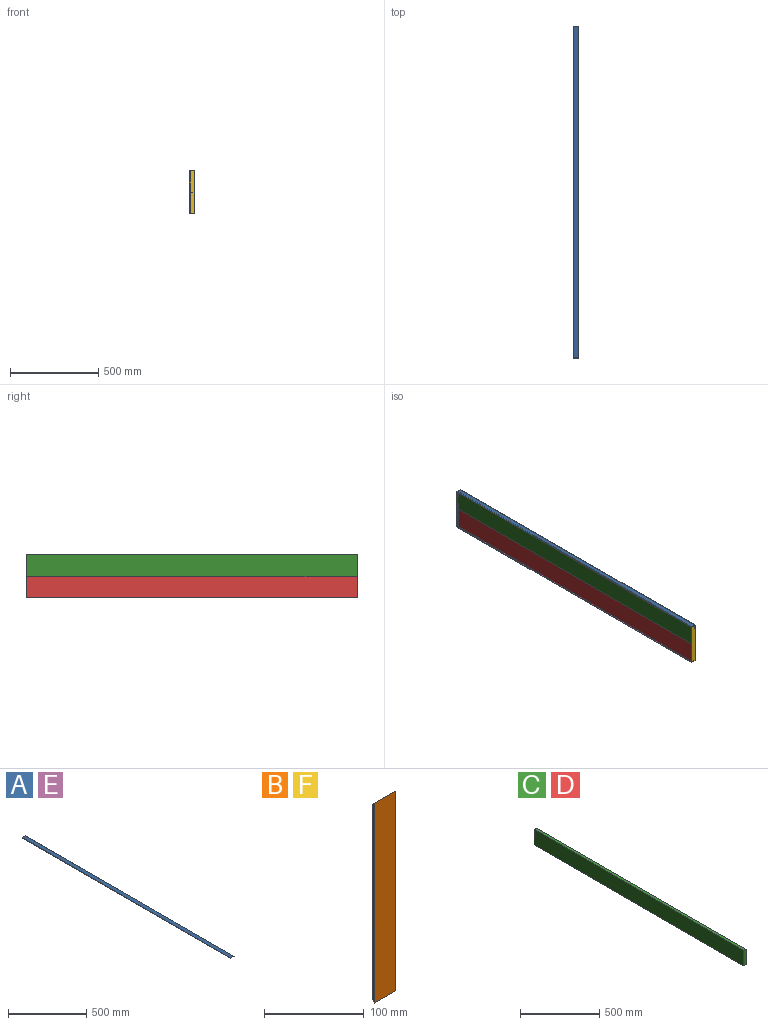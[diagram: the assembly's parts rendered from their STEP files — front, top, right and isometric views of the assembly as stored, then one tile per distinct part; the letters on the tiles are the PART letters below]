
ASSEMBLY  parts=6 mates=5
PART A: 8 faces, bbox 30x1880x30 mm
  f0: plane 1820x3mm, normal (0,0,-1), area 5460mm2, adj f1,f4,f6,f7
  f1: plane 1874x27mm, normal (-1,0,0), area 49869mm2, adj f0,f3,f6,f7
  f2: plane 1880x3mm, normal (-1,0,0), area 5631mm2, adj f3,f5,f6,f7
  f3: plane 1874x27mm, normal (0,0,-1), area 50598mm2, adj f1,f2,f6,f7
  f4: plane 1880x30mm, normal (1,0,0), area 55500mm2, adj f0,f5,f6,f7
  f5: plane 1880x30mm, normal (0,0,1), area 56400mm2, adj f2,f4,f6,f7
  f6: plane 30x30mm, normal (0,-0.71,-0.71), area 241.8mm2, adj f0,f1,f2,f3,f4,f5
  f7: plane 30x30mm, normal (0,0.71,-0.71), area 241.8mm2, adj f0,f1,f2,f3,f4,f5
PART B: 8 faces, bbox 30x30x245 mm
  f0: plane 245x30mm, normal (1,0,0), area 6450mm2, adj f1,f5,f6,f7
  f1: plane 185x3mm, normal (0,1,0), area 555mm2, adj f0,f4,f6,f7
  f2: plane 239x27mm, normal (0,1,0), area 6453mm2, adj f3,f4,f6,f7
  f3: plane 245x3mm, normal (-1,0,0), area 726mm2, adj f2,f5,f6,f7
  f4: plane 239x27mm, normal (-1,0,0), area 5724mm2, adj f1,f2,f6,f7
  f5: plane 245x30mm, normal (0,-1,0), area 7350mm2, adj f0,f3,f6,f7
  f6: plane 30x30mm, normal (0,0.71,-0.71), area 241.8mm2, adj f0,f1,f2,f3,f4,f5
  f7: plane 30x30mm, normal (0,0.71,0.71), area 241.8mm2, adj f0,f1,f2,f3,f4,f5
PART C: 6 faces, bbox 20x1872x120 mm
  f0: plane 1872x20mm, normal (0,0,1), area 37440mm2, adj f1,f3,f4,f5
  f1: plane 1872x120mm, normal (-1,0,0), area 224640mm2, adj f0,f2,f4,f5
  f2: plane 1872x20mm, normal (0,0,-1), area 37440mm2, adj f1,f3,f4,f5
  f3: plane 1872x120mm, normal (1,0,0), area 224640mm2, adj f0,f2,f4,f5
  f4: plane 120x20mm, normal (0,1,0), area 2400mm2, adj f0,f1,f2,f3
  f5: plane 120x20mm, normal (0,-1,0), area 2400mm2, adj f0,f1,f2,f3
PART D: same geometry as C
PART E: same geometry as A
PART F: same geometry as B
PLACE A t=(-316.61,-1070.99,274.59)mm
PLACE B rot(axis=(-1,0,0),180deg) t=(-320.74,511.46,254.34)mm
PLACE C t=(-50.09,-1065.99,346.11)mm
PLACE D t=(-50.09,-1065.99,226.11)mm
PLACE E rot(axis=(1,0,0),180deg) t=(-316.61,809.01,-10.91)mm
PLACE F t=(-320.74,-773.45,9.34)mm
MATE fastened D.f0 <-> C.f2  axis (0,0,1) through (-491.25,806.01,131.34)mm
MATE fastened C.f4 <-> B.f2  axis (0,1,0) through (-491.25,806.01,251.34)mm
MATE fastened E.f7 <-> F.f6  axis (0,-0.71,0.71) through (-491.25,-1067.99,12.34)mm
MATE fastened B.f6 <-> A.f7  axis (0,-0.71,0.71) through (-491.25,806.01,251.34)mm
MATE fastened F.f7 <-> A.f6  axis (0,0.71,0.71) through (-491.25,-1067.99,251.34)mm
